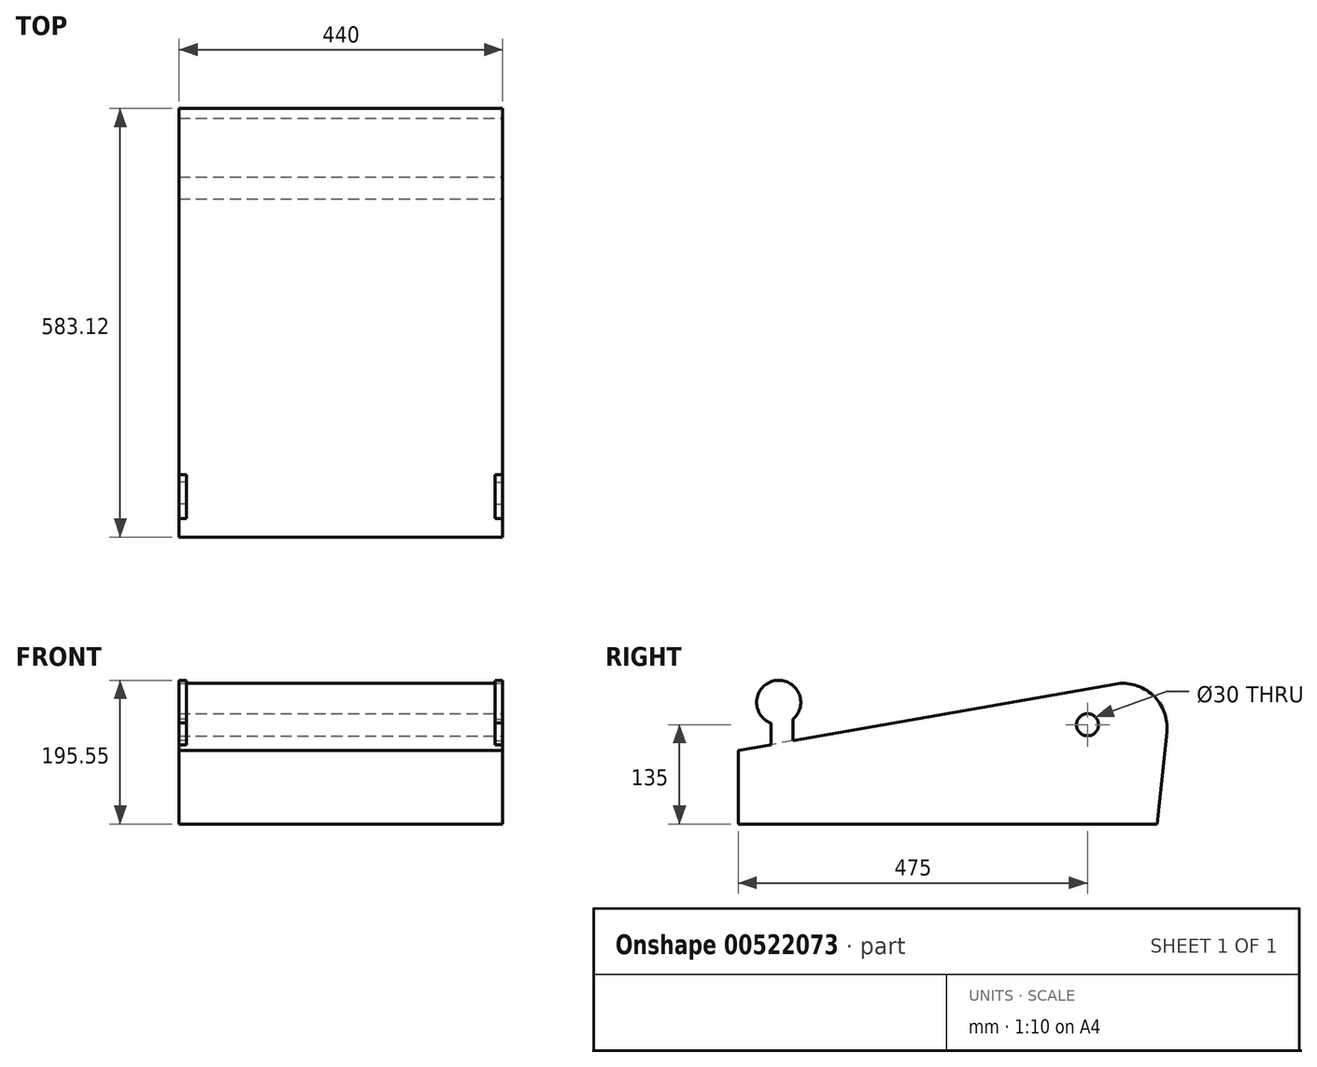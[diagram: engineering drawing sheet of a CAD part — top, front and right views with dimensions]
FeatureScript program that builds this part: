
annotation { "Feature Type Name" : "Feature", "Feature Type Description" : "" }
export const myFeature = defineFeature(function(context is Context, id is Id, definition is map)
    precondition{}
    {
        {
            var Q0;
            Q0=qCreatedBy(makeId("Right.planeOp"),FACE);
            var sketch = newSketch(context, id + "F0", { "sketchPlane" : qUnion([Q0])});
            skLineSegment(sketch, "E0", {"start": v(0, 0) * mm, "end": v(570, 0) * mm});
            skLineSegment(sketch, "E1", {"start": v(570, 0) * mm, "end": v(582.8, 125.2) * mm});
            skLineSegment(sketch, "E2", {"start": v(512.7, 190.4) * mm, "end": v(0, 100) * mm});
            skLineSegment(sketch, "E3", {"start": v(0, 100) * mm, "end": v(0, 0) * mm});
            skPoint(sketch, "E4.visualSharp", {"position": v(590.88, 204.19) * mm});
            skArc(sketch, "E4.filletArc", {"start": v(582.8, 125.2) * mm, "mid": v(563.98, 175.25) * mm, "end": v(512.7, 190.4) * mm});
            skCircle(sketch, "E5", {"center": v(475, 135) * mm, "radius": 15 * mm});
            skSolve(sketch);
        }
        {
            var Q0;
            Q0=makeQuery(id+"F0.imprint","IMPRINT",FACE,{"disambiguationData":[TD([[makeQuery(id+"F0.imprint","IMPRINT",EDGE,{"derivedFrom":sQuery(id+"F0.wireOp",EDGE,"E0")}),1.0]])]});
            extrude(context, id + "F1", {"entities" : qUnion([Q0]), "oppositeDirection" : true, "depth" : (440 / 2) * mm, "offsetDistance" : 25 * mm, "hasSecondDirection" : true, "secondDirectionOppositeDirection" : false, "secondDirectionDepth" : 220 * mm});
        }
        {
            var Q0;
            Q0=makeQuery(id+"F1.opExtrude","CAP_FACE",FACE,{"disambiguationData":[OSD([sQuery(id+"F0.wireOp",EDGE,"E0"),sQuery(id+"F0.wireOp",EDGE,"E1"),sQuery(id+"F0.wireOp",EDGE,"E2"),sQuery(id+"F0.wireOp",EDGE,"E3"),sQuery(id+"F0.wireOp",EDGE,"E4.filletArc")])],"isStart":true});
            var sketch = newSketch(context, id + "F2", { "sketchPlane" : qUnion([Q0])});
            skLineSegment(sketch, "E6", {"start": v(44.49, 107.84) * mm, "end": v(44.49, 137.45) * mm});
            skLineSegment(sketch, "E7", {"start": v(74.49, 113.13) * mm, "end": v(74.49, 142.74) * mm});
            skArc(sketch, "E8", {"start": v(74.49, 142.74) * mm, "mid": v(49.8, 195.1) * mm, "end": v(44.49, 137.45) * mm});
            skSolve(sketch);
        }
        {
            var Q0;
            {var subQ0=sQuery(id+"F2.wireOp",EDGE,"E6");Q0=makeQuery(id+"F2.imprint","IMPRINT",FACE,{"disambiguationData":[TD([[makeQuery(id+"F2.imprint","IMPRINT",EDGE,{"derivedFrom":subQ0}),-1.0]])]});}
            extrude(context, id + "F3", {"entities" : qUnion([Q0]), "operationType" : NewBodyOperationType.ADD, "oppositeDirection" : true, "depth" : 10 * mm, "offsetDistance" : 25 * mm});
        }
        {
            var Q0;
            Q0=makeQuery(id+"F1.opExtrude","SWEPT_BODY",BODY,{"disambiguationData":[OSD([sQuery(id+"F0.wireOp",EDGE,"E0"),sQuery(id+"F0.wireOp",EDGE,"E1"),sQuery(id+"F0.wireOp",EDGE,"E2"),sQuery(id+"F0.wireOp",EDGE,"E3"),sQuery(id+"F0.wireOp",EDGE,"E4.filletArc")])]});
            var Q1;
            Q1=qCreatedBy(makeId("Right.planeOp"),FACE);
            mirror(context, id + "F4", {"operationType" : NewBodyOperationType.ADD, "entities" : qUnion([Q0]), "mirrorPlane" : qUnion([Q1])});
        }
    });
